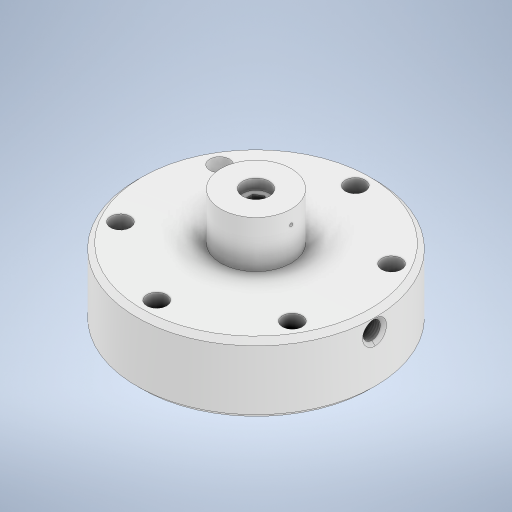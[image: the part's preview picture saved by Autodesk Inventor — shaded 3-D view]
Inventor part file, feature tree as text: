
AUTODESK INVENTOR PART (.ipt)
format: ipt  version: 2023 (Build 270158030, 158C)  size: 430,080 bytes
history: native  units: in
note: dims shown in document units (in); Inventor stores cm internally (conversion verified against a paired STEP export)
features: sketch x13, extrude x4, hole x4, plane x4, chamfer x2, sweep x2, pattern_circular x1, other x1, projected_geometry x1
ambient origin geometry x8: Origin, YZ Plane, XZ Plane, XY Plane, X Axis, Y Axis, Z Axis, Center Point
bodies: Solid1 (feature_tree)
feature tree (32):
  extrude  "Main Body"  Depth=1.75in TaperAngle=0.0deg
  hole  "M5 Bolt"  [1 undecoded]
  pattern_circular  "Circular Pattern1"  Count=6 Angle=360.0deg
  other  "Membrane Cutout"
  chamfer  "Chamfer1"  Distance=0.125in Angle=45.0deg
  sketch  "Sketch5"  dims[d33=0.125in d45=0.1in]
  plane  "Work Plane1"
  sweep  "Sweep2"
  plane  "Work Plane4"
  hole  "Hole7"  [1 undecoded]
  extrude  "Extrusion2"  Depth=0.9449in
  extrude  "Extrusion3"  TaperAngle=0.0deg  [1 undecoded]
  extrude  "Extrusion4"  Depth=0.0246in
  plane  "Work Plane2"
  hole  "Hole5"  [1 undecoded]
  sketch  "Sketch12"  dims[d73=0.3937in d74=0.0in d75=0.0in]
  plane  "Work Plane3"
  sweep  "Sweep3"
  hole  "Hole6"  [1 undecoded]
  chamfer  "Chamfer2"  Distance=0.5in
  sketch  "Sketch1"  dims[d0=6.0in d1=1.75in d2=0.0in]
  sketch  "Sketch2"  dims[d3=0.22in d4=0.75in d5=0.5in d6=1.0in d7=0.5635in d8=0.9798in d9=0.0in d10=2.5in d11=2.3622in d12=360.0deg]
  sketch  "Sketch3"  dims[d17=360.0deg d30=0.125in d31=0.125in d32=45.0deg]
  sketch  "Sketch7"  dims[d46=0.0in d47=0.0in d57=0.56in]
  sketch  "Sketch10"  dims[d59=1.1811in d60=0.0in]
  sketch  "Sketch11"  dims[d61=0.0787in d62=0.2362in d63=0.1181in d64=0.0787in d65=90.0deg d66=0.6167in d67=0.8108in d72=0.9449in]
  projected_geometry  "Projected Loop1"
  sketch  "Sketch13"  dims[d76=0.3937in]
  sketch  "Sketch14"  dims[d77=0.422in d78=0.3389in d79=0.2756in d80=0.0787in d81=90.0deg d82=0.6167in d83=0.8108in d84=0.0246in d85=0.426in d86=1.7717in]
  sketch  "Sketch15"  dims[d87=0.375in d88=0.2756in d89=0.0in]
  sketch  "Sketch16"  dims[d90=0.1083in d91=0.6689in]
  sketch  "Sketch18"  dims[d92=0.2638in d93=0.0in d94=0.3445in d95=0.5in d96=0.8in d98=2.6772in d99=0.7874in d100=0.25in d101=0.2362in d102=0.1575in d103=0.0787in d104=90.0deg d105=0.26in d106=0.8108in d107=2.25in d108=0.5in d109=0.25in d110=0.0787in d111=0.0787in d112=45.0deg]
note: 5 required parameter values undecoded (feature->parameter linkage not recoverable at this tier; creation-order binding heuristic only, values carry confidence <= 0.55)
